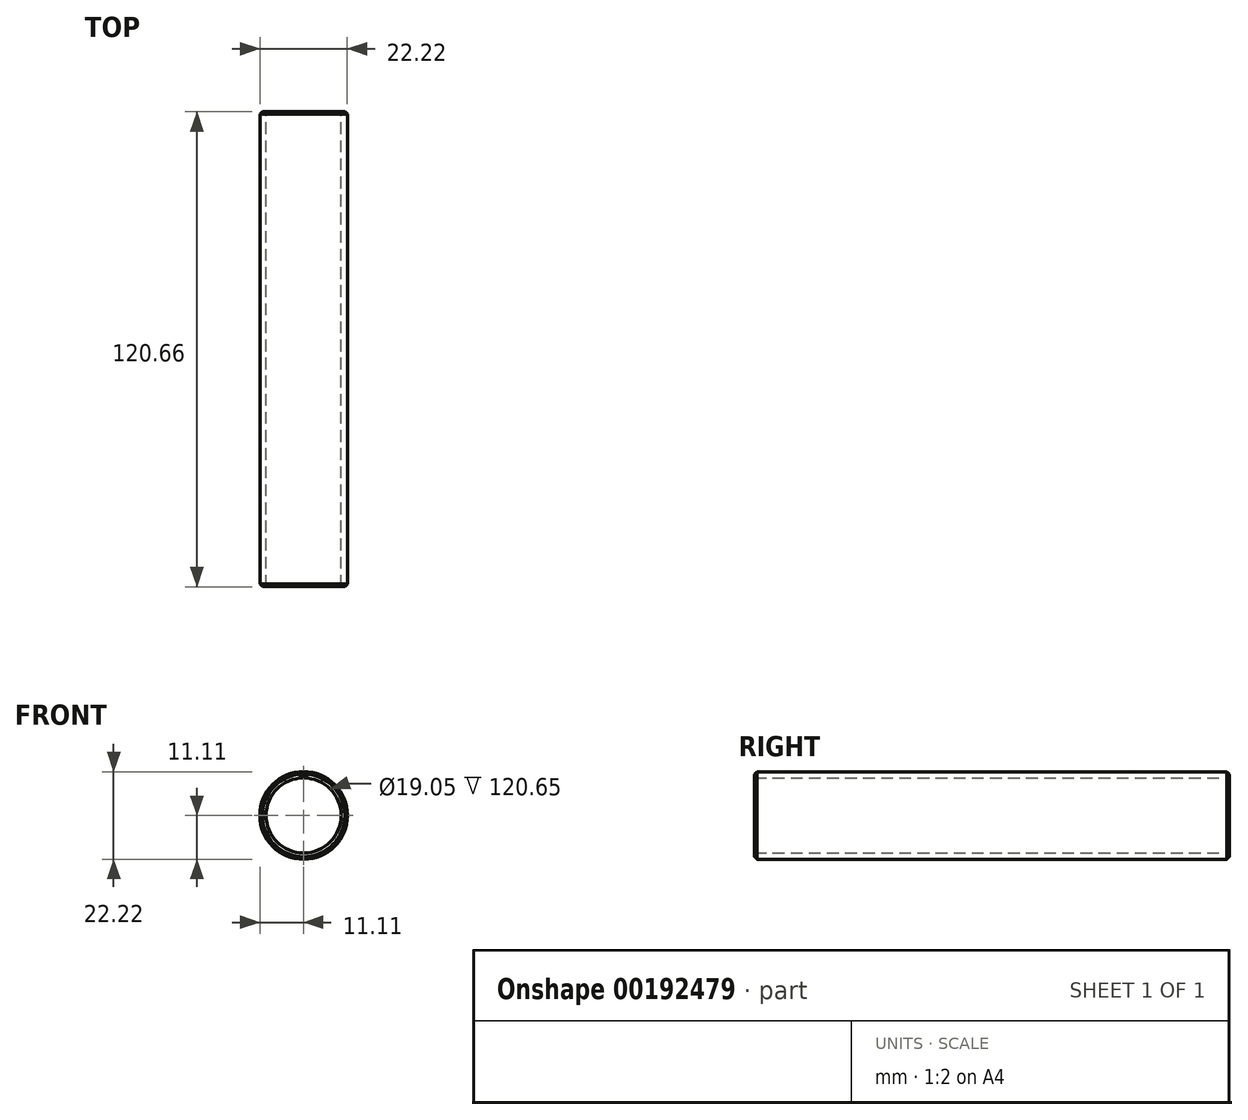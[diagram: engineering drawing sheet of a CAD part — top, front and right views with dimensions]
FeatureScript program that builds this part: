
annotation { "Feature Type Name" : "Feature", "Feature Type Description" : "" }
export const myFeature = defineFeature(function(context is Context, id is Id, definition is map)
    precondition{}
    {
        {
            var Q0;
            Q0=qCreatedBy(makeId("Front.planeOp"),FACE);
            var sketch = newSketch(context, id + "F0", { "sketchPlane" : qUnion([Q0])});
            skCircle(sketch, "E0", {"center": v(0, 0) * mm, "radius": 11.11 * mm});
            skCircle(sketch, "E1", {"center": v(0, 0) * mm, "radius": 9.53 * mm});
            skSolve(sketch);
        }
        {
            var Q0;
            Q0 = qSketchRegion(id + "F0", true);
            extrude(context, id + "F1", {"entities" : qUnion([Q0]), "endBound" : BoundingType.SYMMETRIC, "depth" : 120.65 * mm});
        }
        {
            var Q0;
            Q0=makeQuery(id+"F1.opExtrude","CAP_EDGE",EDGE,{"disambiguationData":[OSD([sQuery(id+"F0.wireOp",EDGE,"E0")])],"isStart":false});
            var Q1;
            Q1=makeQuery(id+"F1.opExtrude","CAP_EDGE",EDGE,{"disambiguationData":[OSD([sQuery(id+"F0.wireOp",EDGE,"E0")])],"isStart":true});
            chamfer(context, id + "F2", {"entities" : qUnion([Q0, Q1]), "width" : 0.64 * mm, "tangentPropagation" : true});
        }
    });
